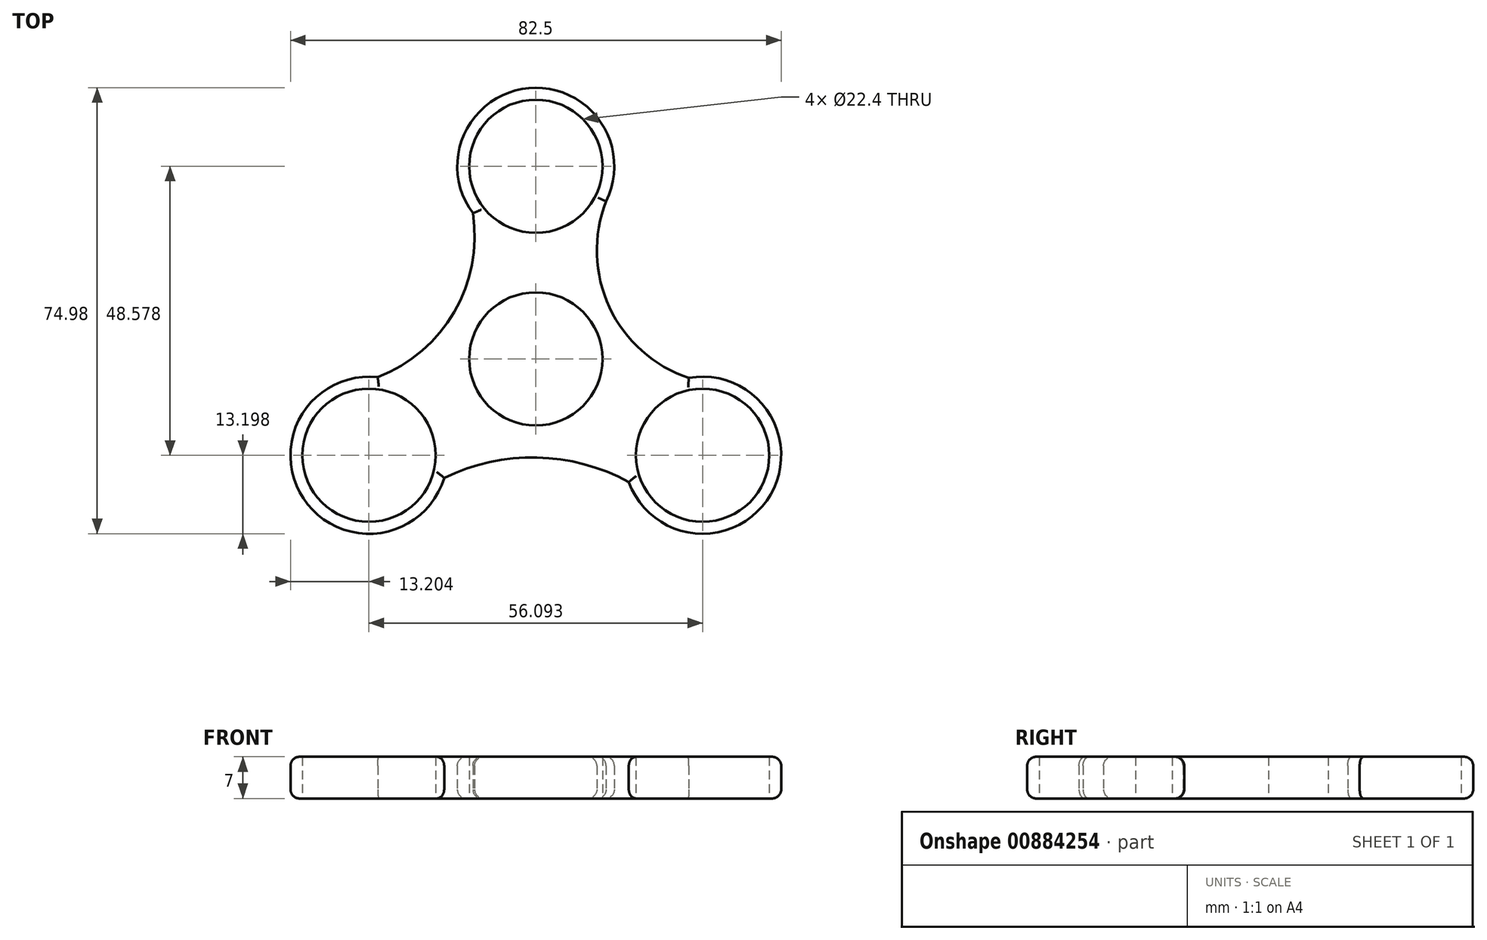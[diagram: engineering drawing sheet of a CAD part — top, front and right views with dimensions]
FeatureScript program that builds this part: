
annotation { "Feature Type Name" : "Feature", "Feature Type Description" : "" }
export const myFeature = defineFeature(function(context is Context, id is Id, definition is map)
    precondition{}
    {
        {
            var Q0;
            Q0=qCreatedBy(makeId("Top.planeOp"),FACE);
            var sketch = newSketch(context, id + "F0", { "sketchPlane" : qUnion([Q0])});
            skCircle(sketch, "E0", {"center": v(0, 0) * mm, "radius": 11.2 * mm});
            skCircle(sketch, "E1", {"center": v(0, 32.39) * mm, "radius": 11.2 * mm});
            skArc(sketch, "E2", {"start": v(11.82, 26.5) * mm, "mid": v(-1.18, 45.53) * mm, "end": v(-10.58, 24.5) * mm});
            skArc(sketch, "E3.1.0", {"start": v(-26.58, -3.07) * mm, "mid": v(-39.06, -23.46) * mm, "end": v(-15.4, -20) * mm});
            skCircle(sketch, "E3.1.1", {"center": v(-28.05, -16.2) * mm, "radius": 11.2 * mm});
            skArc(sketch, "E3.2.0", {"start": v(15.63, -20.69) * mm, "mid": v(39.48, -22.79) * mm, "end": v(25.72, -3.2) * mm});
            skCircle(sketch, "E3.2.1", {"center": v(28.05, -16.2) * mm, "radius": 11.2 * mm});
            skArc(sketch, "E4", {"start": v(15.63, -20.69) * mm, "mid": v(0.2, -16.57) * mm, "end": v(-15.4, -20) * mm});
            skArc(sketch, "E5", {"start": v(-26.58, -3.07) * mm, "mid": v(-13.72, 7.89) * mm, "end": v(-10.58, 24.5) * mm});
            skArc(sketch, "E6", {"start": v(11.82, 26.5) * mm, "mid": v(12.4, 8.67) * mm, "end": v(25.72, -3.2) * mm});
            skSolve(sketch);
        }
        {
            var Q0;
            Q0=makeQuery(id+"F0.imprint","IMPRINT",FACE,{"disambiguationData":[TD([[makeQuery(id+"F0.imprint","IMPRINT",EDGE,{"derivedFrom":sQuery(id+"F0.wireOp",EDGE,"E0")}),-1.0]])]});
            extrude(context, id + "F1", {"entities" : qUnion([Q0]), "depth" : 7 * mm, "offsetDistance" : 25 * mm});
        }
        {
            var Q0;
            Q0=makeQuery(id+"F1.opExtrude","CAP_EDGE",EDGE,{"disambiguationData":[OSD([sQuery(id+"F0.wireOp",EDGE,"E4")])],"isStart":false});
            var Q1;
            Q1=makeQuery(id+"F1.opExtrude","CAP_EDGE",EDGE,{"disambiguationData":[OSD([sQuery(id+"F0.wireOp",EDGE,"E3.1.0")])],"isStart":false});
            var Q2;
            Q2=makeQuery(id+"F1.opExtrude","CAP_EDGE",EDGE,{"disambiguationData":[OSD([sQuery(id+"F0.wireOp",EDGE,"E5")])],"isStart":false});
            var Q3;
            Q3=makeQuery(id+"F1.opExtrude","CAP_EDGE",EDGE,{"disambiguationData":[OSD([sQuery(id+"F0.wireOp",EDGE,"E2")])],"isStart":false});
            var Q4;
            Q4=makeQuery(id+"F1.opExtrude","CAP_EDGE",EDGE,{"disambiguationData":[OSD([sQuery(id+"F0.wireOp",EDGE,"E6")])],"isStart":false});
            var Q5;
            Q5=makeQuery(id+"F1.opExtrude","CAP_EDGE",EDGE,{"disambiguationData":[OSD([sQuery(id+"F0.wireOp",EDGE,"E3.2.0")])],"isStart":false});
            var Q6;
            Q6=makeQuery(id+"F1.opExtrude","CAP_EDGE",EDGE,{"disambiguationData":[OSD([sQuery(id+"F0.wireOp",EDGE,"E6")])],"isStart":true});
            var Q7;
            Q7=makeQuery(id+"F1.opExtrude","CAP_EDGE",EDGE,{"disambiguationData":[OSD([sQuery(id+"F0.wireOp",EDGE,"E2")])],"isStart":true});
            var Q8;
            Q8=makeQuery(id+"F1.opExtrude","CAP_EDGE",EDGE,{"disambiguationData":[OSD([sQuery(id+"F0.wireOp",EDGE,"E5")])],"isStart":true});
            var Q9;
            Q9=makeQuery(id+"F1.opExtrude","CAP_EDGE",EDGE,{"disambiguationData":[OSD([sQuery(id+"F0.wireOp",EDGE,"E3.1.0")])],"isStart":true});
            var Q10;
            Q10=makeQuery(id+"F1.opExtrude","CAP_EDGE",EDGE,{"disambiguationData":[OSD([sQuery(id+"F0.wireOp",EDGE,"E4")])],"isStart":true});
            var Q11;
            Q11=makeQuery(id+"F1.opExtrude","CAP_EDGE",EDGE,{"disambiguationData":[OSD([sQuery(id+"F0.wireOp",EDGE,"E3.2.0")])],"isStart":true});
            fillet(context, id + "F2", {"entities" : qUnion([Q0, Q1, Q2, Q3, Q4, Q5, Q6, Q7, Q8, Q9, Q10, Q11]), "radius" : 1.5 * mm, "tangentPropagation" : true, "allowEdgeOverflow" : false});
        }
    });
